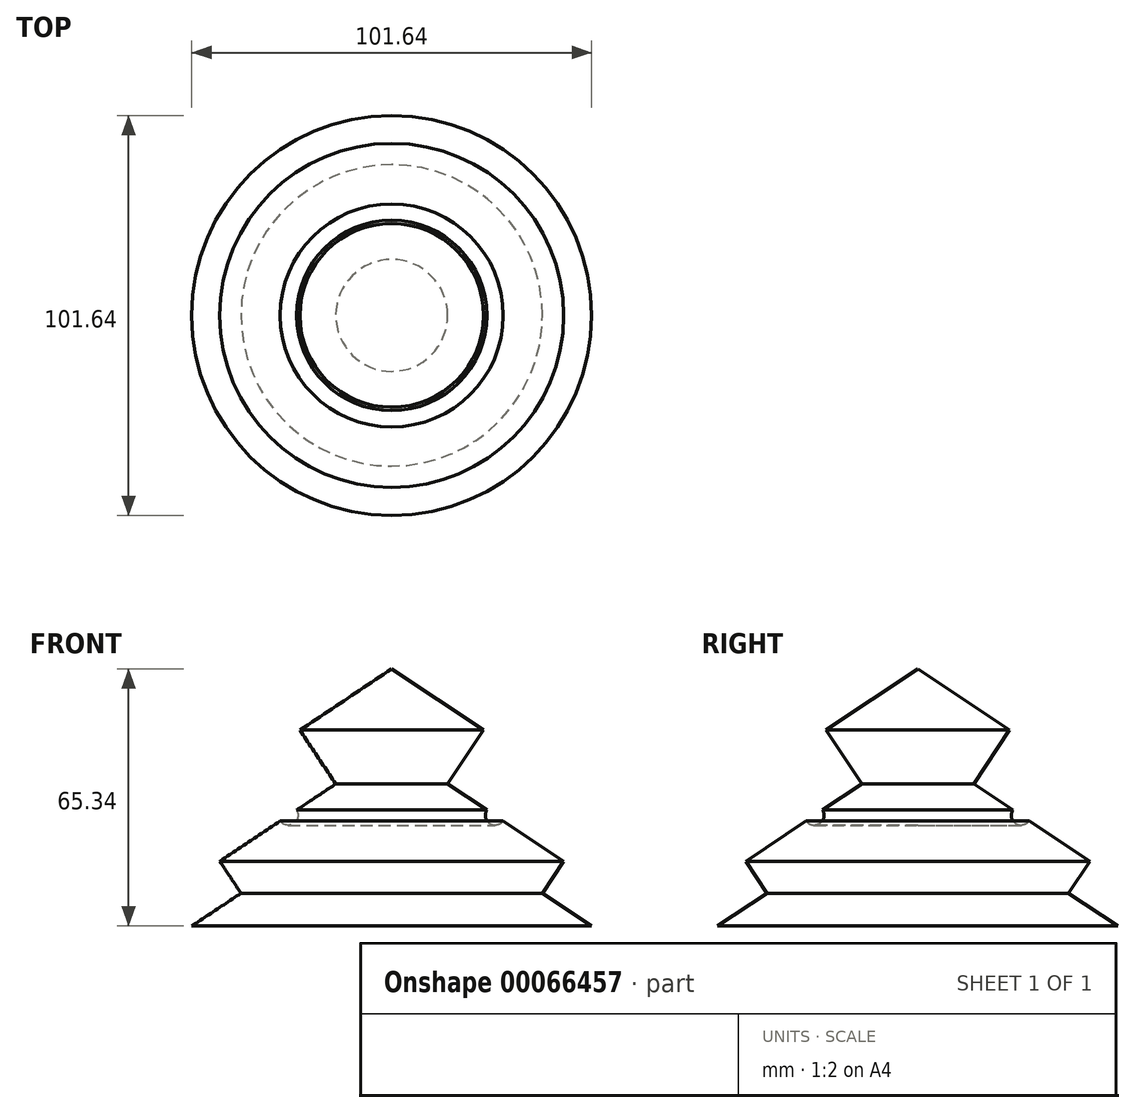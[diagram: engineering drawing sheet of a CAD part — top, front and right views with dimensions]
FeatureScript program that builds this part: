
annotation { "Feature Type Name" : "Feature", "Feature Type Description" : "" }
export const myFeature = defineFeature(function(context is Context, id is Id, definition is map)
    precondition{}
    {
        {
            var Q0;
            Q0=qCreatedBy(makeId("Front.planeOp"),FACE);
            var sketch = newSketch(context, id + "F0", { "sketchPlane" : qUnion([Q0])});
            skLineSegment(sketch, "E0", {"start": v(0, 0) * mm, "end": v(0, 65.34) * mm});
            skLineSegment(sketch, "E1", {"start": v(0, 65.34) * mm, "end": v(23.33, 49.8) * mm});
            skLineSegment(sketch, "E2", {"start": v(23.33, 49.8) * mm, "end": v(14.22, 36.12) * mm});
            skLineSegment(sketch, "E3", {"start": v(14.22, 36.12) * mm, "end": v(43.7, 16.48) * mm});
            skLineSegment(sketch, "E4", {"start": v(43.7, 16.48) * mm, "end": v(38.28, 8.36) * mm});
            skLineSegment(sketch, "E5", {"start": v(38.28, 8.36) * mm, "end": v(50.82, 0) * mm});
            skLineSegment(sketch, "E6", {"start": v(50.82, 0) * mm, "end": v(0, 0) * mm});
            skSolve(sketch);
        }
        {
            var Q0;
            Q0 = qSketchRegion(id + "F0", true);
            var Q1;
            Q1=sQuery(id+"F0.wireOp",EDGE,"E0");
            revolve(context, id + "F1", {"entities" : qUnion([Q0]), "axis" : qUnion([Q1]), "revolveType" : RevolveType.FULL});
        }
        {
            var Q0;
            Q0=qCreatedBy(makeId("Right.planeOp"),FACE);
            var sketch = newSketch(context, id + "F2", { "sketchPlane" : qUnion([Q0])});
            skCircle(sketch, "E7", {"center": v(26.29, 28.14) * mm, "radius": 2.5 * mm});
            skSolve(sketch);
        }
        {
            var Q0;
            Q0=makeQuery(id+"F2.imprint","IMPRINT",FACE,{"disambiguationData":[TD([[makeQuery(id+"F2.imprint","IMPRINT",EDGE,{"derivedFrom":sQuery(id+"F2.wireOp",EDGE,"E7")}),1.0]])]});
            var Q1;
            Q1=sQuery(id+"F0.wireOp",EDGE,"E0");
            revolve(context, id + "F3", {"operationType" : NewBodyOperationType.REMOVE, "entities" : qUnion([Q0]), "axis" : qUnion([Q1]), "revolveType" : RevolveType.FULL, "oppositeDirection" : true});
        }
    });
